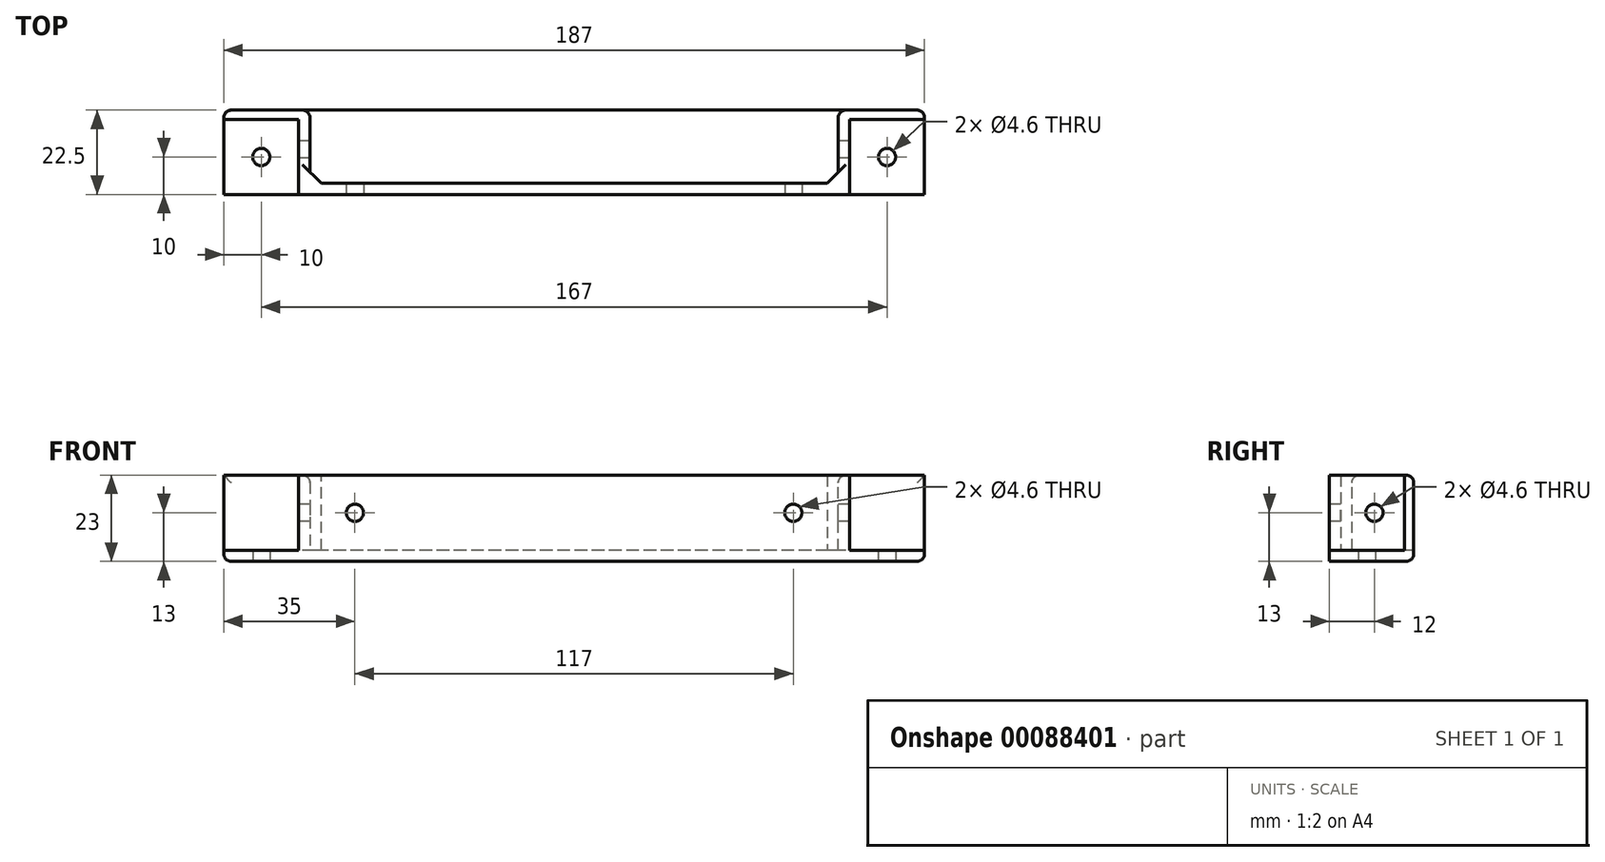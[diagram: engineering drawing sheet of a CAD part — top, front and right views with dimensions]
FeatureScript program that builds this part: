
annotation { "Feature Type Name" : "Feature", "Feature Type Description" : "" }
export const myFeature = defineFeature(function(context is Context, id is Id, definition is map)
    precondition{}
    {
        {
            var Q0;
            Q0=qCreatedBy(makeId("Top.planeOp"),FACE);
            var sketch = newSketch(context, id + "F0", { "sketchPlane" : qUnion([Q0])});
            skLineSegment(sketch, "E0.bottom", {"start": v(93.5, -10) * mm, "end": v(-93.5, -10) * mm});
            skLineSegment(sketch, "E0.top", {"start": v(93.5, 10) * mm, "end": v(-93.5, 10) * mm});
            skLineSegment(sketch, "E0.left", {"start": v(93.5, -10) * mm, "end": v(93.5, 10) * mm});
            skLineSegment(sketch, "E0.right", {"start": v(-93.5, -10) * mm, "end": v(-93.5, 10) * mm});
            skPoint(sketch, "E0.middle", {"position": v(0, 0) * mm});
            skLineSegment(sketch, "E1", {"start": v(-73.5, 10) * mm, "end": v(-73.5, -10) * mm});
            skLineSegment(sketch, "E2", {"start": v(73.5, 10) * mm, "end": v(73.5, -10) * mm});
            skLineSegment(sketch, "E3", {"start": v(93.5, 10) * mm, "end": v(93.5, 12.5) * mm});
            skLineSegment(sketch, "E4", {"start": v(93.5, 12.5) * mm, "end": v(70.5, 12.5) * mm});
            skLineSegment(sketch, "E5", {"start": v(70.5, 12.5) * mm, "end": v(70.5, -7) * mm});
            skLineSegment(sketch, "E6", {"start": v(70.5, -7) * mm, "end": v(-70.5, -7) * mm});
            skLineSegment(sketch, "E7", {"start": v(-70.5, -7) * mm, "end": v(-70.5, 12.5) * mm});
            skLineSegment(sketch, "E8", {"start": v(-70.5, 12.5) * mm, "end": v(-93.5, 12.5) * mm});
            skLineSegment(sketch, "E9", {"start": v(-93.5, 12.5) * mm, "end": v(-93.5, 10) * mm});
            skLineSegment(sketch, "E10", {"start": v(70.5, 12.5) * mm, "end": v(-70.5, 12.5) * mm});
            skSolve(sketch);
        }
        {
            var Q0;
            {var subQ5=sQuery(id+"F0.wireOp",EDGE,"E6");Q0=makeQuery(id+"F0.imprint","IMPRINT",FACE,{"disambiguationData":[TD([[makeQuery(id+"F0.imprint","IMPRINT",EDGE,{"derivedFrom":subQ5}),-1.0]])]});}
            var Q1;
            {var subQ0=sQuery(id+"F0.wireOp",EDGE,"E1");Q1=makeQuery(id+"F0.imprint","IMPRINT",FACE,{"disambiguationData":[TD([[makeQuery(id+"F0.imprint","IMPRINT",EDGE,{"derivedFrom":subQ0}),1.0]])]});}
            var Q2;
            {var subQ0=sQuery(id+"F0.wireOp",EDGE,"E0.right");Q2=makeQuery(id+"F0.imprint","IMPRINT",FACE,{"disambiguationData":[TD([[makeQuery(id+"F0.imprint","IMPRINT",EDGE,{"derivedFrom":subQ0}),-1.0]])]});}
            var Q3;
            {var subQ0=sQuery(id+"F0.wireOp",EDGE,"E8");Q3=makeQuery(id+"F0.imprint","IMPRINT",FACE,{"disambiguationData":[TD([[makeQuery(id+"F0.imprint","IMPRINT",EDGE,{"derivedFrom":subQ0}),1.0]])]});}
            var Q4;
            {var subQ0=sQuery(id+"F0.wireOp",EDGE,"E0.left");Q4=makeQuery(id+"F0.imprint","IMPRINT",FACE,{"disambiguationData":[TD([[makeQuery(id+"F0.imprint","IMPRINT",EDGE,{"derivedFrom":subQ0}),1.0]])]});}
            var Q5;
            {var subQ1=sQuery(id+"F0.wireOp",EDGE,"E3");Q5=makeQuery(id+"F0.imprint","IMPRINT",FACE,{"disambiguationData":[TD([[makeQuery(id+"F0.imprint","IMPRINT",EDGE,{"derivedFrom":subQ1}),1.0]])]});}
            var Q6;
            {var subQ5=sQuery(id+"F0.wireOp",EDGE,"E10");Q6=makeQuery(id+"F0.imprint","IMPRINT",FACE,{"disambiguationData":[TD([[makeQuery(id+"F0.imprint","IMPRINT",EDGE,{"derivedFrom":subQ5}),1.0]])]});}
            extrude(context, id + "F8", {"entities" : qUnion([Q0, Q1, Q2, Q3, Q4, Q5, Q6]), "oppositeDirection" : true, "depth" : 3 * mm});
        }
        {
            var Q0;
            {var subQ0=sQuery(id+"F0.wireOp",EDGE,"E1");Q0=makeQuery(id+"F0.imprint","IMPRINT",FACE,{"disambiguationData":[TD([[makeQuery(id+"F0.imprint","IMPRINT",EDGE,{"derivedFrom":subQ0}),1.0]])]});}
            var Q1;
            {var subQ0=sQuery(id+"F0.wireOp",EDGE,"E8");Q1=makeQuery(id+"F0.imprint","IMPRINT",FACE,{"disambiguationData":[TD([[makeQuery(id+"F0.imprint","IMPRINT",EDGE,{"derivedFrom":subQ0}),1.0]])]});}
            var Q2;
            {var subQ1=sQuery(id+"F0.wireOp",EDGE,"E3");Q2=makeQuery(id+"F0.imprint","IMPRINT",FACE,{"disambiguationData":[TD([[makeQuery(id+"F0.imprint","IMPRINT",EDGE,{"derivedFrom":subQ1}),1.0]])]});}
            extrude(context, id + "F1", {"entities" : qUnion([Q0, Q1, Q2]), "operationType" : NewBodyOperationType.ADD, "depth" : 20 * mm});
        }
        {
            var Q0;
            Q0=makeQuery(id+"F8.opExtrude","CAP_FACE",FACE,{"disambiguationData":[OSD([sQuery(id+"F0.wireOp",EDGE,"E0.bottom"),sQuery(id+"F0.wireOp",EDGE,"E0.top"),sQuery(id+"F0.wireOp",EDGE,"E0.left"),sQuery(id+"F0.wireOp",EDGE,"E0.right"),sQuery(id+"F0.wireOp",EDGE,"E3"),sQuery(id+"F0.wireOp",EDGE,"E4"),sQuery(id+"F0.wireOp",EDGE,"E5"),sQuery(id+"F0.wireOp",EDGE,"E7"),sQuery(id+"F0.wireOp",EDGE,"E8"),sQuery(id+"F0.wireOp",EDGE,"E9")])],"isStart":false});
            var sketch = newSketch(context, id + "F9", { "sketchPlane" : qUnion([Q0])});
            skCircle(sketch, "E11", {"center": v(-83.5, 0) * mm, "radius": 2.3 * mm});
            skCircle(sketch, "E12", {"center": v(83.5, 0) * mm, "radius": 2.3 * mm});
            skSolve(sketch);
        }
        {
            var Q0;
            Q0=makeQuery(id+"F9.imprint","IMPRINT",FACE,{"disambiguationData":[TD([[makeQuery(id+"F9.imprint","IMPRINT",EDGE,{"derivedFrom":sQuery(id+"F9.wireOp",EDGE,"E11")}),1.0]])]});
            var Q1;
            Q1=makeQuery(id+"F9.imprint","IMPRINT",FACE,{"disambiguationData":[TD([[makeQuery(id+"F9.imprint","IMPRINT",EDGE,{"derivedFrom":sQuery(id+"F9.wireOp",EDGE,"E12")}),1.0]])]});
            extrude(context, id + "F10", {"entities" : qUnion([Q0, Q1]), "operationType" : NewBodyOperationType.REMOVE, "endBound" : BoundingType.UP_TO_NEXT, "oppositeDirection" : true, "depth" : 25 * mm});
        }
        {
            var Q0;
            Q0=makeQuery(id+"F1.opExtrude","SWEPT_FACE",FACE,{"disambiguationData":[OSD([sQuery(id+"F0.wireOp",EDGE,"E7")])]});
            var sketch = newSketch(context, id + "F2", { "sketchPlane" : qUnion([Q0])});
            skLineSegment(sketch, "E13.0", {"start": v(-10, 20) * mm, "end": v(-10, 0) * mm, "construction": true});
            skLineSegment(sketch, "E14.0", {"start": v(-10, -3) * mm, "end": v(12.5, -3) * mm, "construction": true});
            skCircle(sketch, "E15", {"center": v(2, 10) * mm, "radius": 2.3 * mm});
            skSolve(sketch);
        }
        {
            var Q0;
            Q0=makeQuery(id+"F2.imprint","IMPRINT",FACE,{"disambiguationData":[TD([[makeQuery(id+"F2.imprint","IMPRINT",EDGE,{"derivedFrom":sQuery(id+"F2.wireOp",EDGE,"E15")}),1.0]])]});
            extrude(context, id + "F3", {"entities" : qUnion([Q0]), "operationType" : NewBodyOperationType.REMOVE, "endBound" : BoundingType.THROUGH_ALL, "depth" : 25 * mm, "hasSecondDirection" : true, "secondDirectionBound" : SecondDirectionBoundingType.THROUGH_ALL, "secondDirectionOppositeDirection" : true, "secondDirectionDepth" : 25 * mm});
        }
        {
            var Q0;
            {var subQ0=sQuery(id+"F0.wireOp",EDGE,"E0.bottom");Q0=makeQuery(id+"F1.boolean.opBoolean","MERGE",FACE,{"derivedFrom":[makeQuery(id+"F8.opExtrude","SWEPT_FACE",FACE,{"disambiguationData":[OSD([subQ0])]}),makeQuery(id+"F1.opExtrude","SWEPT_FACE",FACE,{"disambiguationData":[OSD([subQ0])]})]});}
            var sketch = newSketch(context, id + "F4", { "sketchPlane" : qUnion([Q0])});
            skLineSegment(sketch, "E16", {"start": v(-73.5, 10) * mm, "end": v(73.5, 10) * mm, "construction": true});
            skCircle(sketch, "E17", {"center": v(-58.5, 10) * mm, "radius": 2.3 * mm});
            skCircle(sketch, "E18", {"center": v(58.5, 10) * mm, "radius": 2.3 * mm});
            skSolve(sketch);
        }
        {
            var Q0;
            Q0=makeQuery(id+"F4.imprint","IMPRINT",FACE,{"disambiguationData":[TD([[makeQuery(id+"F4.imprint","IMPRINT",EDGE,{"derivedFrom":sQuery(id+"F4.wireOp",EDGE,"E17")}),1.0]])]});
            var Q1;
            Q1=makeQuery(id+"F4.imprint","IMPRINT",FACE,{"disambiguationData":[TD([[makeQuery(id+"F4.imprint","IMPRINT",EDGE,{"derivedFrom":sQuery(id+"F4.wireOp",EDGE,"E18")}),1.0]])]});
            extrude(context, id + "F5", {"entities" : qUnion([Q0, Q1]), "operationType" : NewBodyOperationType.REMOVE, "endBound" : BoundingType.UP_TO_NEXT, "oppositeDirection" : true, "depth" : 25 * mm});
        }
        {
            var Q0;
            Q0=makeQuery(id+"F1.opExtrude","SWEPT_EDGE",EDGE,{"disambiguationData":[OSD([sQuery(id+"F0.wireOp",EDGE,"E5"),sQuery(id+"F0.wireOp",EDGE,"E6")])]});
            var Q1;
            Q1=makeQuery(id+"F1.opExtrude","CAP_EDGE",EDGE,{"disambiguationData":[OSD([sQuery(id+"F0.wireOp",EDGE,"E5")])],"isStart":true});
            var Q2;
            Q2=makeQuery(id+"F1.opExtrude","SWEPT_EDGE",EDGE,{"disambiguationData":[OSD([sQuery(id+"F0.wireOp",EDGE,"E6"),sQuery(id+"F0.wireOp",EDGE,"E7")])]});
            var Q3;
            Q3=makeQuery(id+"F1.opExtrude","CAP_EDGE",EDGE,{"disambiguationData":[OSD([sQuery(id+"F0.wireOp",EDGE,"E7")])],"isStart":true});
            var Q4;
            Q4=makeQuery(id+"F1.opExtrude","CAP_EDGE",EDGE,{"disambiguationData":[OSD([sQuery(id+"F0.wireOp",EDGE,"E6")])],"isStart":true});
            chamfer(context, id + "F6", {"entities" : qUnion([Q0, Q1, Q2, Q3, Q4]), "width" : 3 * mm, "tangentPropagation" : true});
        }
        {
            var Q0;
            {var subQ0=sQuery(id+"F0.wireOp",EDGE,"E8");var subQ1=sQuery(id+"F0.wireOp",EDGE,"E7");Q0=makeQuery(id+"F1.boolean.opBoolean","MERGE",EDGE,{"derivedFrom":[makeQuery(id+"F8.opExtrude","SWEPT_EDGE",EDGE,{"disambiguationData":[OSD([subQ1,subQ0])]}),makeQuery(id+"F1.opExtrude","SWEPT_EDGE",EDGE,{"disambiguationData":[OSD([subQ1,subQ0])]})]});}
            var Q1;
            Q1=makeQuery(id+"F8.opExtrude","CAP_EDGE",EDGE,{"disambiguationData":[OSD([sQuery(id+"F0.wireOp",EDGE,"E8")])],"isStart":false});
            var Q2;
            {var subQ0=sQuery(id+"F0.wireOp",EDGE,"E9");var subQ1=sQuery(id+"F0.wireOp",EDGE,"E8");Q2=makeQuery(id+"F1.boolean.opBoolean","MERGE",EDGE,{"derivedFrom":[makeQuery(id+"F8.opExtrude","SWEPT_EDGE",EDGE,{"disambiguationData":[OSD([subQ1,subQ0])]}),makeQuery(id+"F1.opExtrude","SWEPT_EDGE",EDGE,{"disambiguationData":[OSD([subQ1,subQ0])]})]});}
            var Q3;
            Q3=makeQuery(id+"F1.opExtrude","CAP_EDGE",EDGE,{"disambiguationData":[OSD([sQuery(id+"F0.wireOp",EDGE,"E8")])],"isStart":false});
            var Q4;
            Q4=makeQuery(id+"F1.opExtrude","CAP_EDGE",EDGE,{"disambiguationData":[OSD([sQuery(id+"F0.wireOp",EDGE,"E4")])],"isStart":false});
            var Q5;
            {var subQ0=sQuery(id+"F0.wireOp",EDGE,"E4");var subQ1=sQuery(id+"F0.wireOp",EDGE,"E3");Q5=makeQuery(id+"F1.boolean.opBoolean","MERGE",EDGE,{"derivedFrom":[makeQuery(id+"F8.opExtrude","SWEPT_EDGE",EDGE,{"disambiguationData":[OSD([subQ1,subQ0])]}),makeQuery(id+"F1.opExtrude","SWEPT_EDGE",EDGE,{"disambiguationData":[OSD([subQ1,subQ0])]})]});}
            var Q6;
            Q6=makeQuery(id+"F8.opExtrude","CAP_EDGE",EDGE,{"disambiguationData":[OSD([sQuery(id+"F0.wireOp",EDGE,"E4")])],"isStart":false});
            var Q7;
            {var subQ0=sQuery(id+"F0.wireOp",EDGE,"E5");var subQ1=sQuery(id+"F0.wireOp",EDGE,"E4");Q7=makeQuery(id+"F1.boolean.opBoolean","MERGE",EDGE,{"derivedFrom":[makeQuery(id+"F8.opExtrude","SWEPT_EDGE",EDGE,{"disambiguationData":[OSD([subQ1,subQ0])]}),makeQuery(id+"F1.opExtrude","SWEPT_EDGE",EDGE,{"disambiguationData":[OSD([subQ1,subQ0])]})]});}
            var Q8;
            Q8=makeQuery(id+"F8.opExtrude","CAP_EDGE",EDGE,{"disambiguationData":[OSD([sQuery(id+"F0.wireOp",EDGE,"E0.left"),sQuery(id+"F0.wireOp",EDGE,"E3")])],"isStart":false});
            var Q9;
            Q9=makeQuery(id+"F8.opExtrude","CAP_EDGE",EDGE,{"disambiguationData":[OSD([sQuery(id+"F0.wireOp",EDGE,"E0.right"),sQuery(id+"F0.wireOp",EDGE,"E9")])],"isStart":false});
            var Q10;
            Q10=makeQuery(id+"F1.opExtrude","SWEPT_EDGE",EDGE,{"disambiguationData":[OSD([sQuery(id+"F0.wireOp",EDGE,"E4"),sQuery(id+"F0.wireOp",EDGE,"E5"),sQuery(id+"F0.wireOp",EDGE,"E10")])]});
            var Q11;
            Q11=makeQuery(id+"F1.opExtrude","SWEPT_EDGE",EDGE,{"disambiguationData":[OSD([sQuery(id+"F0.wireOp",EDGE,"E7"),sQuery(id+"F0.wireOp",EDGE,"E8"),sQuery(id+"F0.wireOp",EDGE,"E10")])]});
            var Q12;
            Q12=makeQuery(id+"F1.opExtrude","CAP_EDGE",EDGE,{"disambiguationData":[OSD([sQuery(id+"F0.wireOp",EDGE,"E7")])],"isStart":false});
            var Q13;
            Q13=makeQuery(id+"F1.opExtrude","CAP_EDGE",EDGE,{"disambiguationData":[OSD([sQuery(id+"F0.wireOp",EDGE,"E5")])],"isStart":false});
            fillet(context, id + "F7", {"entities" : qUnion([Q0, Q1, Q2, Q3, Q4, Q5, Q6, Q7, Q8, Q9, Q10, Q11, Q12, Q13]), "radius" : 2 * mm, "tangentPropagation" : true, "allowEdgeOverflow" : false});
        }
    });
